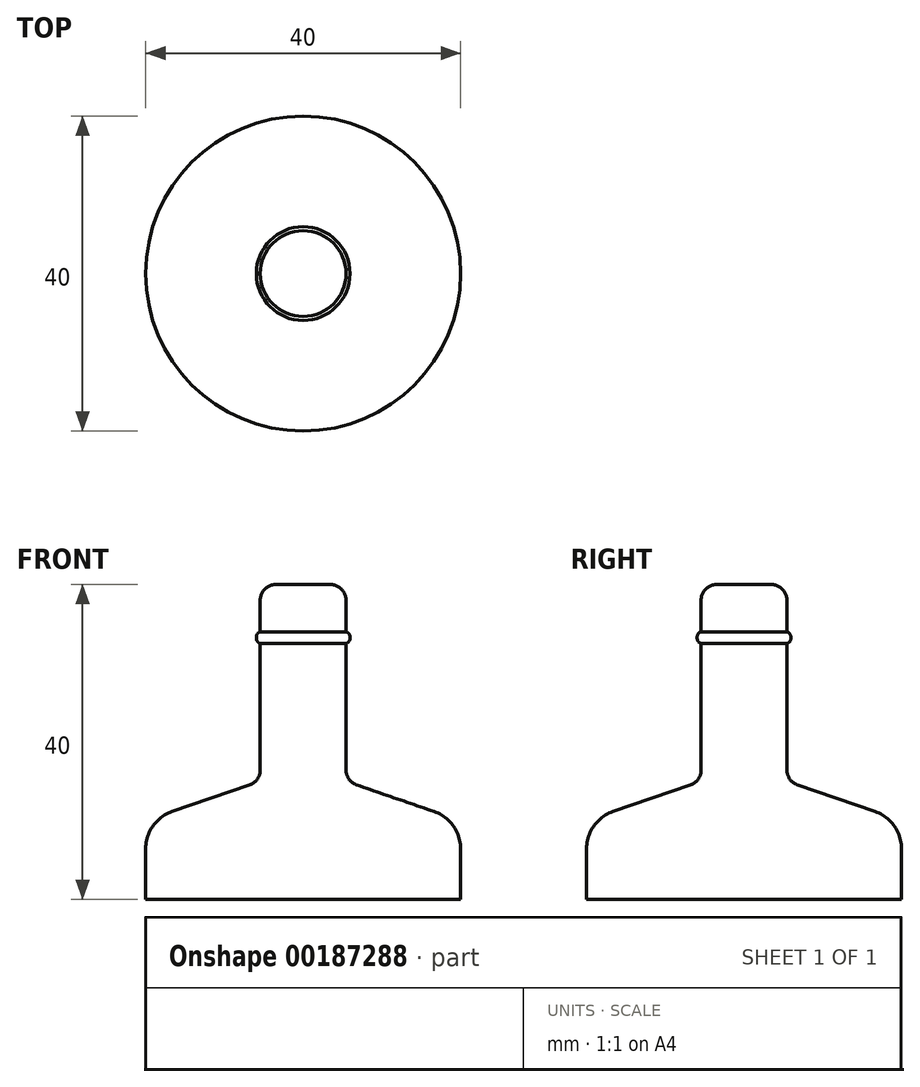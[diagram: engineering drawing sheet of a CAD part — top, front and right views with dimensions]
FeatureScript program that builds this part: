
annotation { "Feature Type Name" : "Feature", "Feature Type Description" : "" }
export const myFeature = defineFeature(function(context is Context, id is Id, definition is map)
    precondition{}
    {
        {
            var Q0;
            Q0=qCreatedBy(makeId("Front.planeOp"),FACE);
            var sketch = newSketch(context, id + "F0", { "sketchPlane" : qUnion([Q0])});
            skLineSegment(sketch, "E0", {"start": v(0, 0) * mm, "end": v(0, 40) * mm});
            skLineSegment(sketch, "E1", {"start": v(0, 40) * mm, "end": v(5.45, 40) * mm});
            skLineSegment(sketch, "E2", {"start": v(5.45, 40) * mm, "end": v(5.45, 15) * mm});
            skLineSegment(sketch, "E3", {"start": v(0, 0) * mm, "end": v(20, 0) * mm});
            skLineSegment(sketch, "E4", {"start": v(20, 0) * mm, "end": v(20, 10) * mm});
            skLineSegment(sketch, "E5", {"start": v(20, 10) * mm, "end": v(5.45, 15) * mm});
            skPoint(sketch, "E6", {"position": v(5.45, 34) * mm});
            skPoint(sketch, "E7", {"position": v(5.45, 32.5) * mm});
            skLineSegment(sketch, "E8", {"start": v(5.45, 34) * mm, "end": v(5.95, 34) * mm});
            skLineSegment(sketch, "E9", {"start": v(5.45, 32.5) * mm, "end": v(5.95, 32.5) * mm});
            skLineSegment(sketch, "E10", {"start": v(5.95, 32.5) * mm, "end": v(5.95, 34) * mm});
            skSolve(sketch);
        }
        {
            var Q0;
            Q0=makeQuery(id+"F0.imprint","IMPRINT",FACE,{"disambiguationData":[TD([[makeQuery(id+"F0.imprint","IMPRINT",EDGE,{"derivedFrom":sQuery(id+"F0.wireOp",EDGE,"E0")}),-1.0]])]});
            var Q1;
            {var subQ0=sQuery(id+"F0.wireOp",EDGE,"E8");Q1=makeQuery(id+"F0.imprint","IMPRINT",FACE,{"disambiguationData":[TD([[makeQuery(id+"F0.imprint","IMPRINT",EDGE,{"derivedFrom":subQ0}),-1.0]])]});}
            var Q2;
            Q2=sQuery(id+"F0.wireOp",EDGE,"E0");
            revolve(context, id + "F1", {"entities" : qUnion([Q0, Q1]), "axis" : qUnion([Q2]), "revolveType" : RevolveType.FULL});
        }
        {
            var Q0;
            Q0=makeQuery(id+"F1.opRevolve","SWEPT_EDGE",EDGE,{"disambiguationData":[OSD([sQuery(id+"F0.wireOp",EDGE,"E1"),sQuery(id+"F0.wireOp",EDGE,"E2")])]});
            var Q1;
            Q1=makeQuery(id+"F1.opRevolve","SWEPT_EDGE",EDGE,{"disambiguationData":[OSD([sQuery(id+"F0.wireOp",EDGE,"E2"),sQuery(id+"F0.wireOp",EDGE,"E5")])]});
            fillet(context, id + "F2", {"entities" : qUnion([Q0, Q1]), "radius" : 2 * mm, "tangentPropagation" : true, "allowEdgeOverflow" : false});
        }
        {
            var Q0;
            Q0=makeQuery(id+"F1.opRevolve","SWEPT_EDGE",EDGE,{"disambiguationData":[OSD([sQuery(id+"F0.wireOp",EDGE,"E4"),sQuery(id+"F0.wireOp",EDGE,"E5")])]});
            fillet(context, id + "F3", {"entities" : qUnion([Q0]), "radius" : 5 * mm, "tangentPropagation" : true, "allowEdgeOverflow" : false});
        }
        {
            var Q0;
            Q0=makeQuery(id+"F1.opRevolve","SWEPT_FACE",FACE,{"disambiguationData":[OSD([sQuery(id+"F0.wireOp",EDGE,"E10")])]});
            fillet(context, id + "F4", {"entities" : qUnion([Q0]), "radius" : 0.7 * mm, "tangentPropagation" : true, "allowEdgeOverflow" : false});
        }
    });
